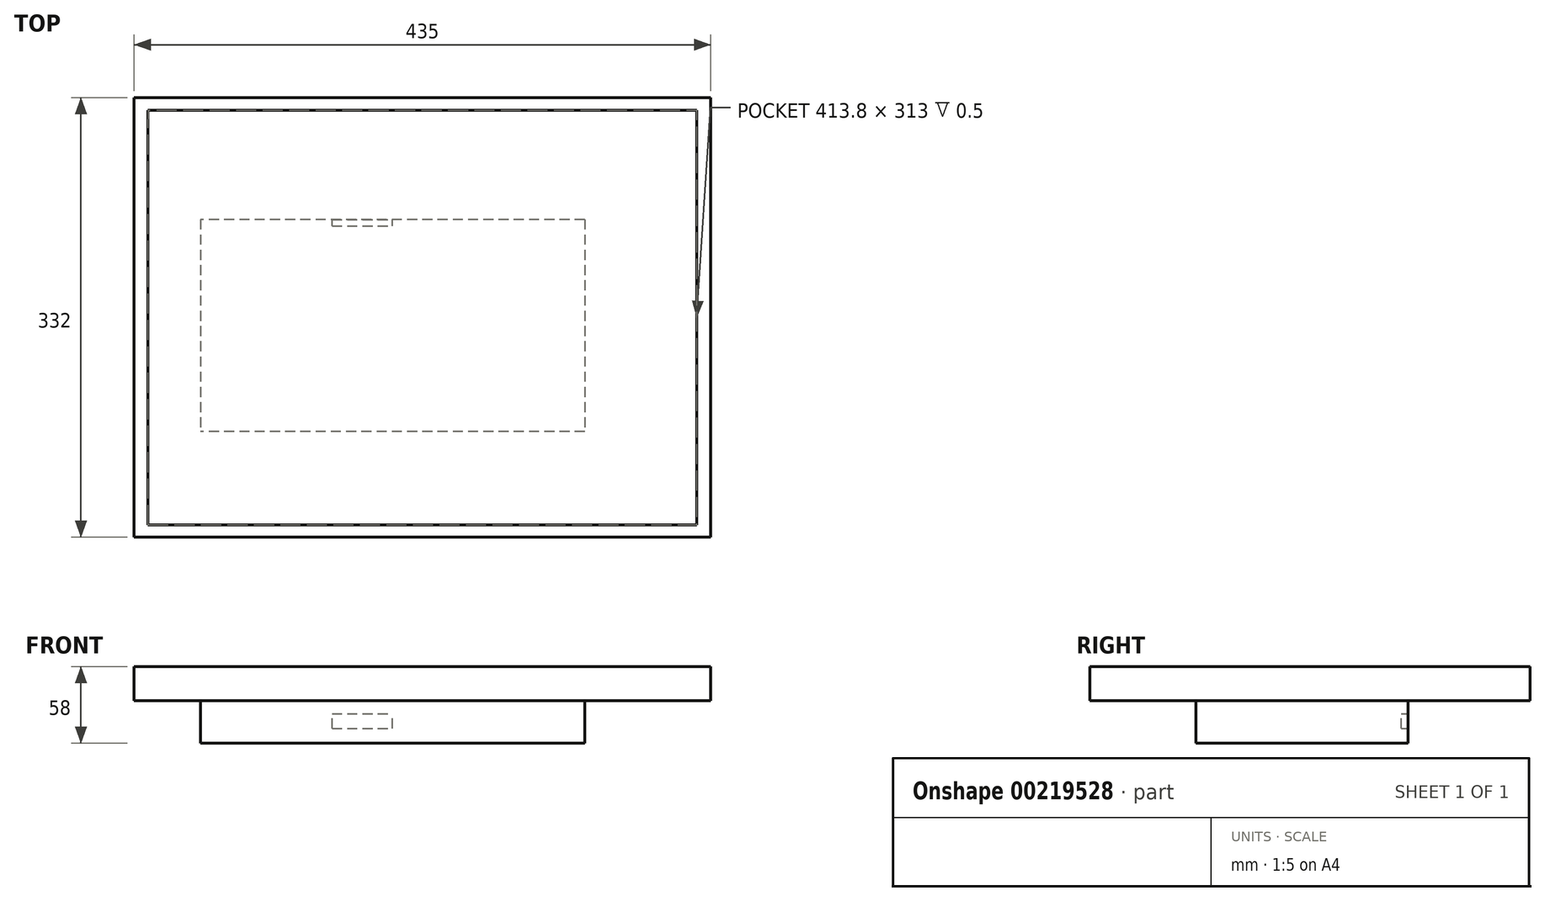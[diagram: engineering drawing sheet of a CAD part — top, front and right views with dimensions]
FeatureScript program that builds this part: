
annotation { "Feature Type Name" : "Feature", "Feature Type Description" : "" }
export const myFeature = defineFeature(function(context is Context, id is Id, definition is map)
    precondition{}
    {
        {
            var Q0;
            Q0=qCreatedBy(makeId("Top.planeOp"),FACE);
            var sketch = newSketch(context, id + "F0", { "sketchPlane" : qUnion([Q0])});
            skLineSegment(sketch, "E0.bottom", {"start": v(-217.5, -166) * mm, "end": v(217.5, -166) * mm});
            skLineSegment(sketch, "E0.top", {"start": v(-217.5, 166) * mm, "end": v(217.5, 166) * mm});
            skLineSegment(sketch, "E0.left", {"start": v(-217.5, -166) * mm, "end": v(-217.5, 166) * mm});
            skLineSegment(sketch, "E0.right", {"start": v(217.5, -166) * mm, "end": v(217.5, 166) * mm});
            skPoint(sketch, "E0.middle", {"position": v(0, 0) * mm});
            skSolve(sketch);
        }
        {
            var Q0;
            Q0 = qSketchRegion(id + "F0", true);
            extrude(context, id + "F1", {"entities" : qUnion([Q0]), "depth" : 26 * mm});
        }
        {
            var Q0;
            Q0=makeQuery(id+"F1.opExtrude","CAP_FACE",FACE,{"disambiguationData":[OSD([sQuery(id+"F0.wireOp",EDGE,"E0.bottom"),sQuery(id+"F0.wireOp",EDGE,"E0.top"),sQuery(id+"F0.wireOp",EDGE,"E0.left"),sQuery(id+"F0.wireOp",EDGE,"E0.right")])],"isStart":false});
            var sketch = newSketch(context, id + "F2", { "sketchPlane" : qUnion([Q0])});
            skLineSegment(sketch, "E1.bottom", {"start": v(-206.9, 156.5) * mm, "end": v(206.9, 156.5) * mm});
            skLineSegment(sketch, "E1.top", {"start": v(-206.9, -156.5) * mm, "end": v(206.9, -156.5) * mm});
            skLineSegment(sketch, "E1.left", {"start": v(-206.9, 156.5) * mm, "end": v(-206.9, -156.5) * mm});
            skLineSegment(sketch, "E1.right", {"start": v(206.9, 156.5) * mm, "end": v(206.9, -156.5) * mm});
            skSolve(sketch);
        }
        {
            var Q0;
            Q0=makeQuery(id+"F2.imprint","IMPRINT",FACE,{"disambiguationData":[TD([[makeQuery(id+"F2.imprint","IMPRINT",EDGE,{"derivedFrom":sQuery(id+"F2.wireOp",EDGE,"E1.bottom")}),-1.0]])]});
            extrude(context, id + "F3", {"entities" : qUnion([Q0]), "operationType" : NewBodyOperationType.REMOVE, "oppositeDirection" : true, "depth" : 0.5 * mm});
        }
        {
            var Q0;
            Q0=makeQuery(id+"F0.imprint","IMPRINT",FACE,{"disambiguationData":[TD([[makeQuery(id+"F0.imprint","IMPRINT",EDGE,{"derivedFrom":sQuery(id+"F0.wireOp",EDGE,"E0.bottom")}),1.0]])]});
            var sketch = newSketch(context, id + "F4", { "sketchPlane" : qUnion([Q0])});
            skLineSegment(sketch, "E2.bottom", {"start": v(122.5, 74) * mm, "end": v(-167.5, 74) * mm});
            skLineSegment(sketch, "E2.top", {"start": v(122.5, -86) * mm, "end": v(-167.5, -86) * mm});
            skLineSegment(sketch, "E2.left", {"start": v(122.5, 74) * mm, "end": v(122.5, -86) * mm});
            skLineSegment(sketch, "E2.right", {"start": v(-167.5, 74) * mm, "end": v(-167.5, -86) * mm});
            skSolve(sketch);
        }
        {
            var Q0;
            Q0 = qSketchRegion(id + "F4", true);
            extrude(context, id + "F5", {"entities" : qUnion([Q0]), "operationType" : NewBodyOperationType.ADD, "oppositeDirection" : true, "depth" : 32 * mm});
        }
        {
            var Q0;
            Q0=makeQuery(id+"F5.opExtrude","SWEPT_FACE",FACE,{"disambiguationData":[OSD([sQuery(id+"F4.wireOp",EDGE,"E2.bottom")])]});
            var sketch = newSketch(context, id + "F6", { "sketchPlane" : qUnion([Q0])});
            skPoint(sketch, "E3.oppositeSnap0", {"position": v(22.5, 0) * mm});
            skLineSegment(sketch, "E3.bottom", {"start": v(68.16, -20.72) * mm, "end": v(22.5, -20.72) * mm});
            skLineSegment(sketch, "E3.top", {"start": v(68.16, -9.84) * mm, "end": v(22.5, -9.84) * mm});
            skLineSegment(sketch, "E3.left", {"start": v(68.16, -20.72) * mm, "end": v(68.16, -9.84) * mm});
            skLineSegment(sketch, "E3.right", {"start": v(22.5, -20.72) * mm, "end": v(22.5, -9.84) * mm});
            skSolve(sketch);
        }
        {
            var Q0;
            Q0 = qSketchRegion(id + "F6", true);
            extrude(context, id + "F7", {"entities" : qUnion([Q0]), "operationType" : NewBodyOperationType.REMOVE, "oppositeDirection" : true, "depth" : 5 * mm});
        }
    });
